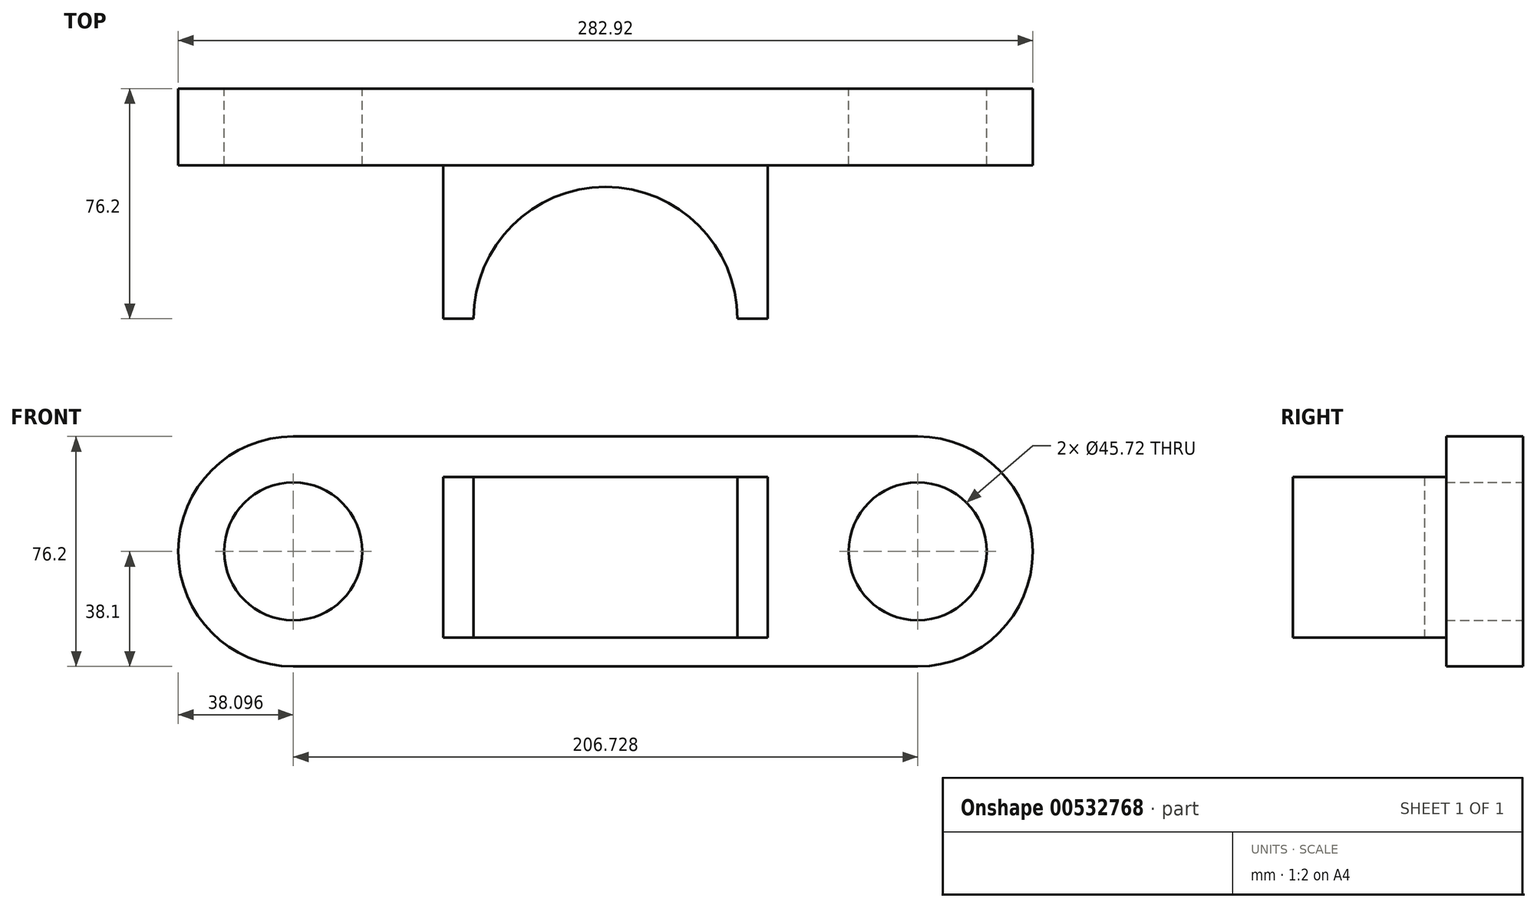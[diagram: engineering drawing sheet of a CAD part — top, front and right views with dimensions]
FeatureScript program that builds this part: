
annotation { "Feature Type Name" : "Feature", "Feature Type Description" : "" }
export const myFeature = defineFeature(function(context is Context, id is Id, definition is map)
    precondition{}
    {
        {
            var Q0;
            Q0=qCreatedBy(makeId("Front.planeOp"),FACE);
            var sketch = newSketch(context, id + "F0", { "sketchPlane" : qUnion([Q0])});
            skLineSegment(sketch, "E0.bottom", {"start": v(-103.36, 38.1) * mm, "end": v(103.36, 38.1) * mm});
            skLineSegment(sketch, "E0.top", {"start": v(-103.36, -38.1) * mm, "end": v(103.36, -38.1) * mm});
            skLineSegment(sketch, "E0.left", {"start": v(-103.36, 38.1) * mm, "end": v(-103.36, -38.1) * mm});
            skLineSegment(sketch, "E0.right", {"start": v(103.36, 38.1) * mm, "end": v(103.36, -38.1) * mm});
            skPoint(sketch, "E0.middle", {"position": v(0, 0) * mm});
            skCircle(sketch, "E1", {"center": v(-103.36, 0) * mm, "radius": 38.1 * mm});
            skPoint(sketch, "E2.center.orphan", {"position": v(62.31, 0) * mm});
            skCircle(sketch, "E3", {"center": v(103.36, 0) * mm, "radius": 38.1 * mm});
            skCircle(sketch, "E4", {"center": v(-103.36, 0) * mm, "radius": 22.86 * mm});
            skCircle(sketch, "E5", {"center": v(103.36, 0) * mm, "radius": 22.86 * mm});
            skSolve(sketch);
        }
        {
            var Q0;
            {var subQ1=sQuery(id+"F0.wireOp",EDGE,"E0.left");var subQ3=sQuery(id+"F0.wireOp",EDGE,"E4");var subQ4=makeQuery(id+"F0.imprint","INTERSECT",VERTEX,{"disambiguationData":[OD(0.0)],"derivedFrom":[subQ1,subQ3]});Q0=makeQuery(id+"F0.imprint","IMPRINT",FACE,{"disambiguationData":[TD([[makeQuery(id+"F0.imprint","IMPRINT",EDGE,{"disambiguationData":[TD([[subQ4,-1.0]])],"derivedFrom":subQ3}),-1.0]])]});}
            var Q1;
            {var subQ1=sQuery(id+"F0.wireOp",EDGE,"E0.right");var subQ3=sQuery(id+"F0.wireOp",EDGE,"E5");var subQ4=makeQuery(id+"F0.imprint","INTERSECT",VERTEX,{"disambiguationData":[OD(0.0)],"derivedFrom":[subQ1,subQ3]});Q1=makeQuery(id+"F0.imprint","IMPRINT",FACE,{"disambiguationData":[TD([[makeQuery(id+"F0.imprint","IMPRINT",EDGE,{"disambiguationData":[TD([[subQ4,1.0]])],"derivedFrom":subQ3}),-1.0]])]});}
            var Q2;
            {var subQ1=sQuery(id+"F0.wireOp",EDGE,"E0.left");var subQ3=sQuery(id+"F0.wireOp",EDGE,"E4");var subQ4=makeQuery(id+"F0.imprint","INTERSECT",VERTEX,{"disambiguationData":[OD(0.0)],"derivedFrom":[subQ1,subQ3]});Q2=makeQuery(id+"F0.imprint","IMPRINT",FACE,{"disambiguationData":[TD([[makeQuery(id+"F0.imprint","IMPRINT",EDGE,{"disambiguationData":[TD([[subQ4,1.0]])],"derivedFrom":subQ3}),-1.0]])]});}
            var Q3;
            {var subQ1=sQuery(id+"F0.wireOp",EDGE,"E0.right");var subQ3=sQuery(id+"F0.wireOp",EDGE,"E5");var subQ4=makeQuery(id+"F0.imprint","INTERSECT",VERTEX,{"disambiguationData":[OD(0.0)],"derivedFrom":[subQ1,subQ3]});Q3=makeQuery(id+"F0.imprint","IMPRINT",FACE,{"disambiguationData":[TD([[makeQuery(id+"F0.imprint","IMPRINT",EDGE,{"disambiguationData":[TD([[subQ4,-1.0]])],"derivedFrom":subQ3}),-1.0]])]});}
            var Q4;
            {var subQ0=sQuery(id+"F0.wireOp",EDGE,"E0.bottom");Q4=makeQuery(id+"F0.imprint","IMPRINT",FACE,{"disambiguationData":[TD([[makeQuery(id+"F0.imprint","IMPRINT",EDGE,{"derivedFrom":subQ0}),-1.0]])]});}
            extrude(context, id + "F1", {"entities" : qUnion([Q0, Q1, Q2, Q3, Q4]), "depth" : 25.4 * mm, "offsetDistance" : 25.4 * mm});
        }
        {
            var Q0;
            Q0=makeQuery(id+"F1.opExtrude","CAP_FACE",FACE,{"disambiguationData":[OSD([sQuery(id+"F0.wireOp",EDGE,"E0.bottom"),sQuery(id+"F0.wireOp",EDGE,"E0.top"),sQuery(id+"F0.wireOp",EDGE,"E1"),sQuery(id+"F0.wireOp",EDGE,"E3"),sQuery(id+"F0.wireOp",EDGE,"E4"),sQuery(id+"F0.wireOp",EDGE,"E5")])],"isStart":false});
            var sketch = newSketch(context, id + "F2", { "sketchPlane" : qUnion([Q0])});
            skLineSegment(sketch, "E6.bottom", {"start": v(-53.76, 24.71) * mm, "end": v(53.76, 24.71) * mm});
            skLineSegment(sketch, "E6.top", {"start": v(-53.76, -28.5) * mm, "end": v(53.76, -28.5) * mm});
            skLineSegment(sketch, "E6.left", {"start": v(-53.76, 24.71) * mm, "end": v(-53.76, -28.5) * mm});
            skLineSegment(sketch, "E6.right", {"start": v(53.76, 24.71) * mm, "end": v(53.76, -28.5) * mm});
            skPoint(sketch, "E6.middle", {"position": v(0, -1.9) * mm});
            skSolve(sketch);
        }
        {
            var Q0;
            Q0=makeQuery(id+"F2.imprint","IMPRINT",FACE,{"disambiguationData":[TD([[makeQuery(id+"F2.imprint","IMPRINT",EDGE,{"derivedFrom":sQuery(id+"F2.wireOp",EDGE,"E6.bottom")}),-1.0]])]});
            extrude(context, id + "F3", {"entities" : qUnion([Q0]), "operationType" : NewBodyOperationType.ADD, "depth" : 50.8 * mm, "offsetDistance" : 25.4 * mm});
        }
        {
            var Q0;
            Q0=makeQuery(id+"F3.opExtrude","SWEPT_FACE",FACE,{"disambiguationData":[OSD([sQuery(id+"F2.wireOp",EDGE,"E6.top")])]});
            var sketch = newSketch(context, id + "F4", { "sketchPlane" : qUnion([Q0])});
            skCircle(sketch, "E7", {"center": v(0, 76.2) * mm, "radius": 43.66 * mm});
            skSolve(sketch);
        }
        {
            var Q0;
            Q0 = qSketchRegion(id + "F4", true);
            extrude(context, id + "F5", {"entities" : qUnion([Q0]), "operationType" : NewBodyOperationType.REMOVE, "oppositeDirection" : true, "depth" : 203.2 * mm, "offsetDistance" : 25.4 * mm});
        }
    });
